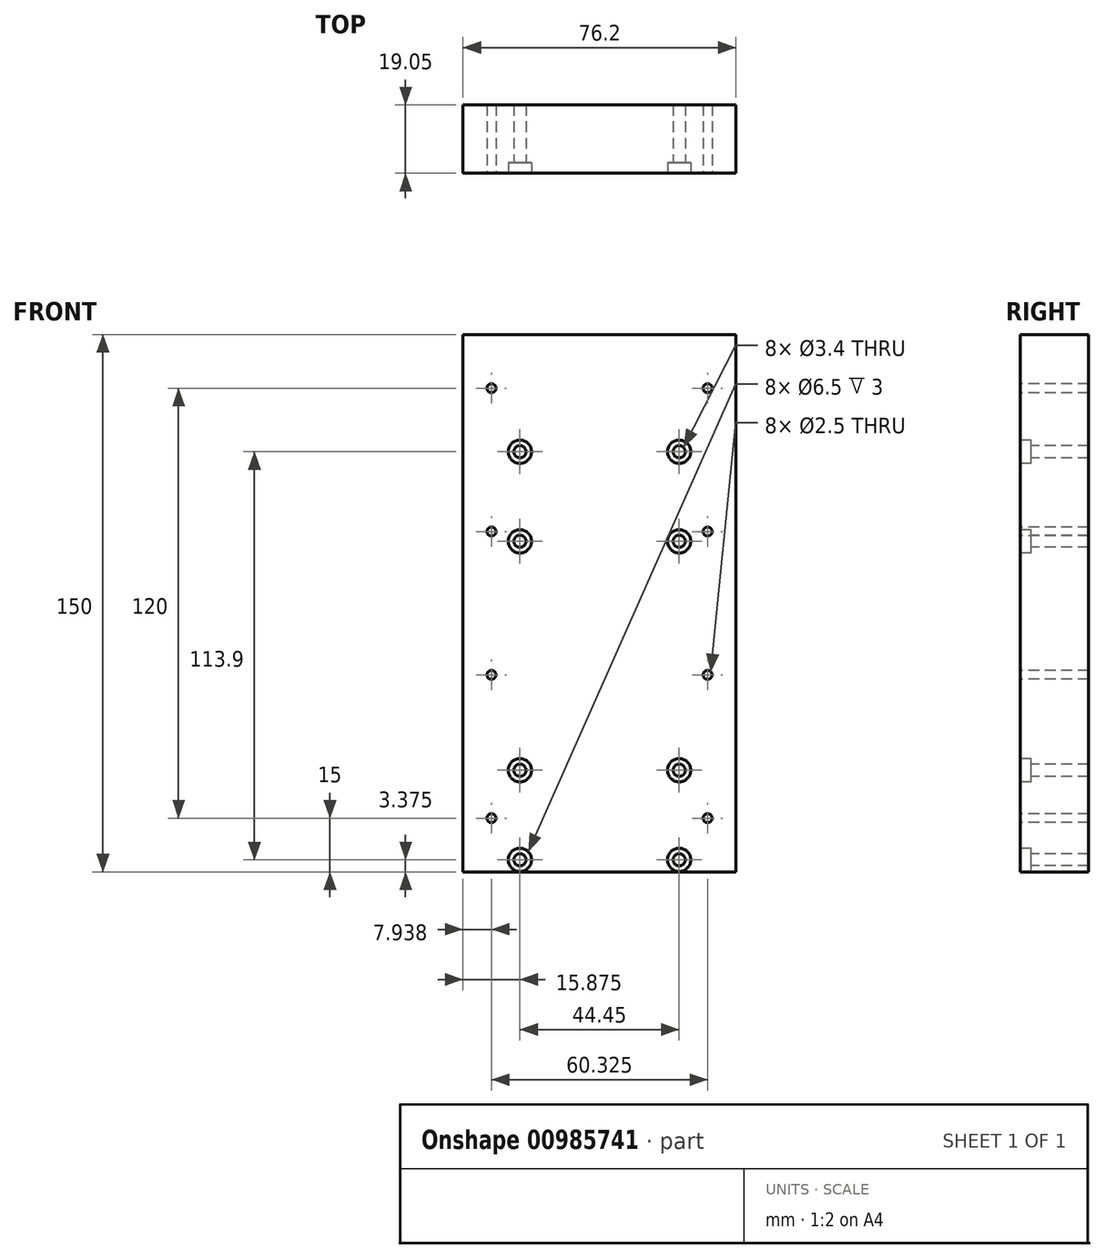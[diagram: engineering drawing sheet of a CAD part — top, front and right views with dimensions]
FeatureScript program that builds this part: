
annotation { "Feature Type Name" : "Feature", "Feature Type Description" : "" }
export const myFeature = defineFeature(function(context is Context, id is Id, definition is map)
    precondition{}
    {
        {
            var Q0;
            Q0=qCreatedBy(makeId("Front.planeOp"),FACE);
            var sketch = newSketch(context, id + "F0", { "sketchPlane" : qUnion([Q0])});
            skLineSegment(sketch, "E0.bottom", {"start": v(0, 0) * mm, "end": v(76.2, 0) * mm});
            skLineSegment(sketch, "E0.top", {"start": v(0, 150) * mm, "end": v(76.2, 150) * mm});
            skLineSegment(sketch, "E0.left", {"start": v(0, 0) * mm, "end": v(0, 150) * mm});
            skLineSegment(sketch, "E0.right", {"start": v(76.2, 0) * mm, "end": v(76.2, 150) * mm});
            skSolve(sketch);
        }
        {
            var Q0;
            Q0 = qSketchRegion(id + "F0", true);
            extrude(context, id + "F1", {"entities" : qUnion([Q0]), "depth" : 19.05 * mm, "offsetDistance" : 25.4 * mm});
        }
        {
            var Q0;
            Q0=makeQuery(id+"F1.opExtrude","CAP_FACE",FACE,{"disambiguationData":[OSD([sQuery(id+"F0.wireOp",EDGE,"E0.bottom"),sQuery(id+"F0.wireOp",EDGE,"E0.top"),sQuery(id+"F0.wireOp",EDGE,"E0.left"),sQuery(id+"F0.wireOp",EDGE,"E0.right")])],"isStart":false});
            var sketch = newSketch(context, id + "F2", { "sketchPlane" : qUnion([Q0])});
            skLineSegment(sketch, "E1", {"start": v(15.87, 117.28) * mm, "end": v(15.87, 92.27) * mm, "construction": true});
            skLineSegment(sketch, "E2", {"start": v(15.87, 92.27) * mm, "end": v(15.88, 28.37) * mm, "construction": true});
            skLineSegment(sketch, "E3", {"start": v(15.88, 28.38) * mm, "end": v(15.88, 3.38) * mm, "construction": true});
            skLineSegment(sketch, "E4", {"start": v(15.87, 3.37) * mm, "end": v(60.32, 3.38) * mm, "construction": true});
            skLineSegment(sketch, "E5", {"start": v(60.32, 3.38) * mm, "end": v(60.32, 28.38) * mm, "construction": true});
            skLineSegment(sketch, "E6", {"start": v(60.32, 28.37) * mm, "end": v(60.32, 92.27) * mm, "construction": true});
            skLineSegment(sketch, "E7", {"start": v(60.32, 92.27) * mm, "end": v(60.32, 117.28) * mm, "construction": true});
            skLineSegment(sketch, "E8", {"start": v(60.32, 117.27) * mm, "end": v(15.87, 117.27) * mm, "construction": true});
            skLineSegment(sketch, "E9", {"start": v(60.32, 92.27) * mm, "end": v(15.87, 92.27) * mm, "construction": true});
            skLineSegment(sketch, "E10", {"start": v(60.32, 28.38) * mm, "end": v(15.87, 28.37) * mm, "construction": true});
            skLineSegment(sketch, "E11", {"start": v(38.1, 117.27) * mm, "end": v(38.1, 150) * mm, "construction": true});
            skLineSegment(sketch, "E12", {"start": v(60.32, 15.88) * mm, "end": v(15.88, 15.87) * mm, "construction": true});
            skLineSegment(sketch, "E13", {"start": v(60.32, 104.78) * mm, "end": v(15.87, 104.78) * mm, "construction": true});
            skSolve(sketch);
        }
        {
            var Q0;
            Q0=sQuery(id+"F2.wireOp",VERTEX,"E1.start");
            var Q1;
            Q1=sQuery(id+"F2.wireOp",VERTEX,"E1.end");
            var Q2;
            Q2=sQuery(id+"F2.wireOp",VERTEX,"E2.end");
            var Q3;
            Q3=sQuery(id+"F2.wireOp",VERTEX,"E3.end");
            var Q4;
            Q4=sQuery(id+"F2.wireOp",VERTEX,"E4.end");
            var Q5;
            Q5=sQuery(id+"F2.wireOp",VERTEX,"E5.end");
            var Q6;
            Q6=sQuery(id+"F2.wireOp",VERTEX,"E6.end");
            var Q7;
            Q7=sQuery(id+"F2.wireOp",VERTEX,"E7.end");
            var Q8;
            Q8=makeQuery(id+"F1.opExtrude","SWEPT_BODY",BODY,{"disambiguationData":[OSD([sQuery(id+"F0.wireOp",EDGE,"E0.bottom"),sQuery(id+"F0.wireOp",EDGE,"E0.top"),sQuery(id+"F0.wireOp",EDGE,"E0.left"),sQuery(id+"F0.wireOp",EDGE,"E0.right")])]});
            hole(context, id + "F3", {"style" : HoleStyle.C_BORE, "endStyle" : HoleEndStyle.THROUGH, "standardTappedOrClearance" : lookupTablePath({ "fit" : "Normal", "standard" : "ISO", "size" : "M3", "type" : "Clearance" }), "standardBlindInLast" : lookupTablePath({ "fit" : "Normal", "standard" : "ISO", "engagement" : "75%", "pitch" : "0.5 mm", "size" : "M3", "type" : "Clearance & tapped" }), "holeDiameter" : 3.4 * mm, "cBoreDiameter" : 6.5 * mm, "cBoreDepth" : 3 * mm, "majorDiameter" : 6.35 * mm, "isTappedThrough" : true, "tappedDepth" : 19.05 * mm, "tapClearance" : 3, "startFromSketch" : true, "locations" : qUnion([Q0, Q1, Q2, Q3, Q4, Q5, Q6, Q7]), "scope" : qUnion([Q8])});
        }
        {
            var Q0;
            Q0=makeQuery(id+"F1.opExtrude","CAP_FACE",FACE,{"disambiguationData":[OSD([sQuery(id+"F0.wireOp",EDGE,"E0.bottom"),sQuery(id+"F0.wireOp",EDGE,"E0.top"),sQuery(id+"F0.wireOp",EDGE,"E0.left"),sQuery(id+"F0.wireOp",EDGE,"E0.right")])],"isStart":false});
            var sketch = newSketch(context, id + "F4", { "sketchPlane" : qUnion([Q0])});
            skLineSegment(sketch, "E14", {"start": v(7.94, 15) * mm, "end": v(7.94, 55) * mm, "construction": true});
            skLineSegment(sketch, "E15", {"start": v(7.94, 55) * mm, "end": v(7.94, 95) * mm, "construction": true});
            skLineSegment(sketch, "E16", {"start": v(7.94, 95) * mm, "end": v(7.94, 135) * mm, "construction": true});
            skLineSegment(sketch, "E17", {"start": v(7.94, 75) * mm, "end": v(0, 75) * mm, "construction": true});
            skLineSegment(sketch, "E18", {"start": v(7.94, 135) * mm, "end": v(68.26, 135) * mm, "construction": true});
            skLineSegment(sketch, "E19", {"start": v(68.26, 135) * mm, "end": v(68.26, 95) * mm, "construction": true});
            skLineSegment(sketch, "E20", {"start": v(68.26, 95) * mm, "end": v(68.26, 55) * mm, "construction": true});
            skLineSegment(sketch, "E21", {"start": v(68.26, 55) * mm, "end": v(68.26, 15) * mm, "construction": true});
            skLineSegment(sketch, "E22", {"start": v(68.26, 15) * mm, "end": v(7.94, 15) * mm, "construction": true});
            skLineSegment(sketch, "E23", {"start": v(68.26, 55) * mm, "end": v(7.94, 55) * mm, "construction": true});
            skLineSegment(sketch, "E24", {"start": v(68.26, 95) * mm, "end": v(7.94, 95) * mm, "construction": true});
            skLineSegment(sketch, "E25", {"start": v(38.1, 135) * mm, "end": v(38.1, 150) * mm, "construction": true});
            skSolve(sketch);
        }
        {
            var Q0;
            Q0=sQuery(id+"F4.wireOp",VERTEX,"E16.end");
            var Q1;
            Q1=sQuery(id+"F4.wireOp",VERTEX,"E15.end");
            var Q2;
            Q2=sQuery(id+"F4.wireOp",VERTEX,"E14.end");
            var Q3;
            Q3=sQuery(id+"F4.wireOp",VERTEX,"E14.start");
            var Q4;
            Q4=sQuery(id+"F4.wireOp",VERTEX,"E21.end");
            var Q5;
            Q5=sQuery(id+"F4.wireOp",VERTEX,"E20.end");
            var Q6;
            Q6=sQuery(id+"F4.wireOp",VERTEX,"E19.end");
            var Q7;
            Q7=sQuery(id+"F4.wireOp",VERTEX,"E18.end");
            var Q8;
            Q8=makeQuery(id+"F1.opExtrude","SWEPT_BODY",BODY,{"disambiguationData":[OSD([sQuery(id+"F0.wireOp",EDGE,"E0.bottom"),sQuery(id+"F0.wireOp",EDGE,"E0.top"),sQuery(id+"F0.wireOp",EDGE,"E0.left"),sQuery(id+"F0.wireOp",EDGE,"E0.right")])]});
            hole(context, id + "F5", {"style" : HoleStyle.SIMPLE, "endStyle" : HoleEndStyle.BLIND, "standardTappedOrClearance" : lookupTablePath({ "standard" : "ISO", "engagement" : "75%", "pitch" : "0.5 mm", "size" : "M3", "type" : "Tapped" }), "standardBlindInLast" : lookupTablePath({ "standard" : "ISO", "fit" : "Normal", "engagement" : "75%", "pitch" : "0.5 mm", "size" : "M3", "type" : "Clearance & tapped" }), "holeDiameter" : 2.5 * mm, "majorDiameter" : 3 * mm, "showTappedDepth" : true, "holeDepth" : 20.55 * mm, "isTappedThrough" : true, "tappedDepth" : 19.05 * mm, "tapClearance" : 3, "startFromSketch" : true, "locations" : qUnion([Q0, Q1, Q2, Q3, Q4, Q5, Q6, Q7]), "scope" : qUnion([Q8])});
        }
    });
